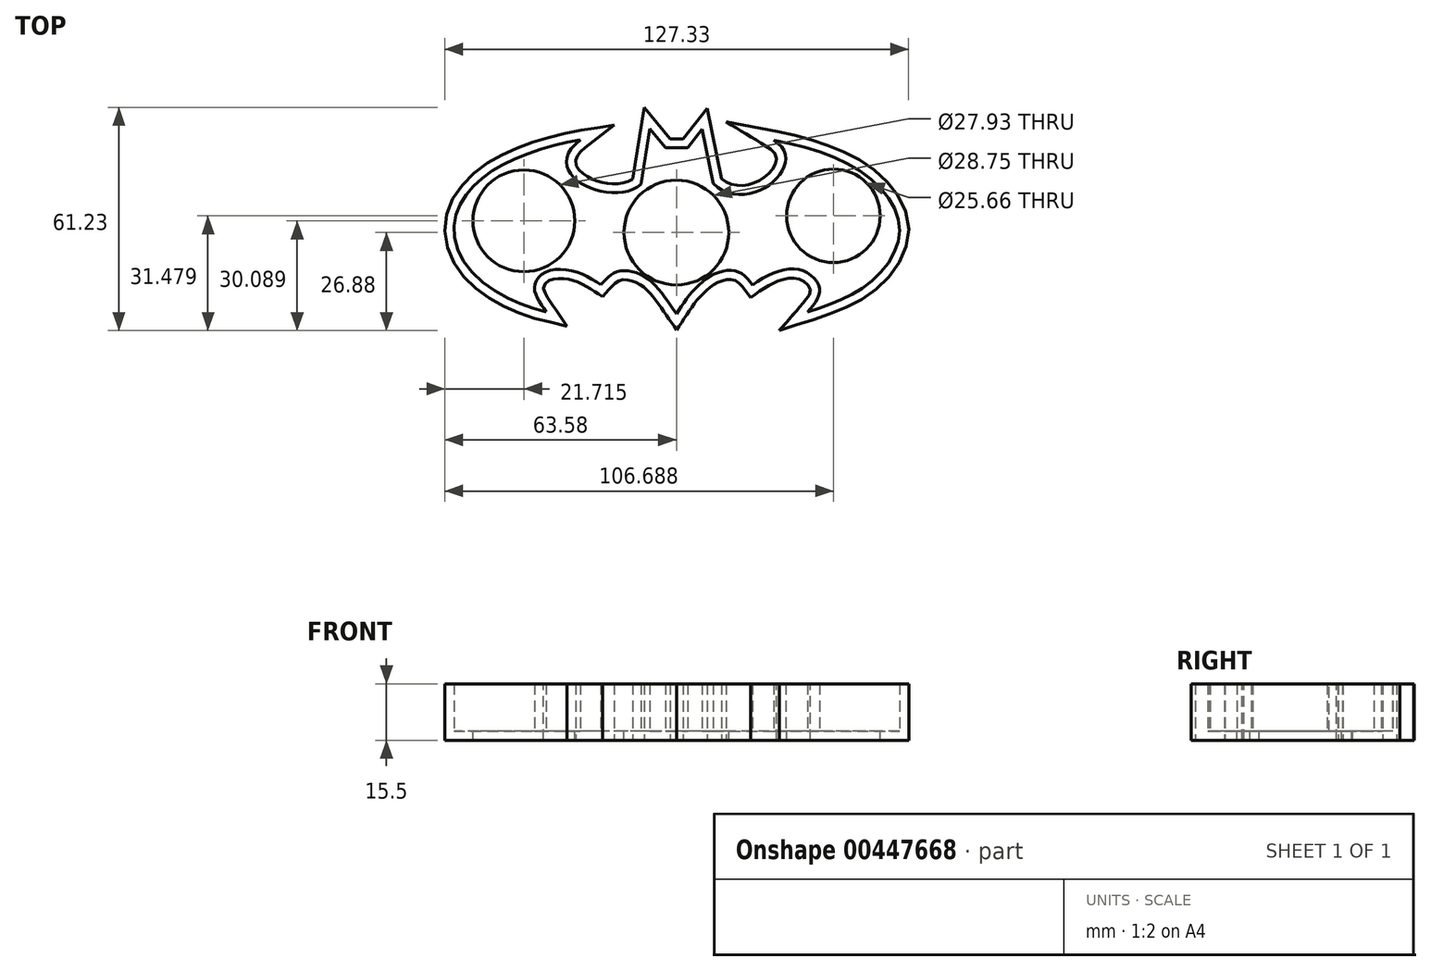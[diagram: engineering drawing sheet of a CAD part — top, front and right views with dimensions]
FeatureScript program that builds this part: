
annotation { "Feature Type Name" : "Feature", "Feature Type Description" : "" }
export const myFeature = defineFeature(function(context is Context, id is Id, definition is map)
    precondition{}
    {
        {
            var Q0;
            Q0=qCreatedBy(makeId("Top.planeOp"),FACE);
            var sketch = newSketch(context, id + "F0", { "sketchPlane" : qUnion([Q0])});
            skLineSegment(sketch, "E0", {"start": v(-2.96, 13.62) * mm, "end": v(3.07, 13.62) * mm});
            skLineSegment(sketch, "E1", {"start": v(7.09, 18.7) * mm, "end": v(3.07, 13.62) * mm});
            skLineSegment(sketch, "E2", {"start": v(-7.25, 18.84) * mm, "end": v(-2.96, 13.62) * mm});
            skLineSegment(sketch, "E3", {"start": v(7.09, 18.7) * mm, "end": v(10.04, 3.84) * mm});
            skLineSegment(sketch, "E4", {"start": v(-7.25, 18.84) * mm, "end": v(-9.66, 3.7) * mm});
            skFitSpline(sketch, "E5", {"points": [v(-9.66, 3.7) * mm, v(-26.35, 15.88) * mm], "startDerivative": vector(-23.41, -20.9) * mm, "endDerivative": vector(37.32, 29.12) * mm});
            skFitSpline(sketch, "E6", {"points": [v(10.04, 3.84) * mm, v(26.7, 15.74) * mm], "startDerivative": vector(29.47, -28.28) * mm, "endDerivative": vector(-31.58, 19.28) * mm});
            skFitSpline(sketch, "E7", {"points": [v(26.7, 15.74) * mm, v(53.14, 5.3) * mm, v(61.23, -9.78) * mm, v(52.21, -24.08) * mm, v(36.04, -31.36) * mm], "startDerivative": vector(99.78, -18.86) * mm, "endDerivative": vector(-72.14, -23.28) * mm});
            skFitSpline(sketch, "E8", {"points": [v(36.04, -31.36) * mm, v(39.31, -25.36) * mm, v(34.1, -19.88) * mm, v(20.9, -24) * mm], "startDerivative": vector(17.69, 20.3) * mm, "endDerivative": vector(-31.55, -22.7) * mm});
            skFitSpline(sketch, "E9", {"points": [v(20.9, -24) * mm, v(16.93, -20.4) * mm, v(10.84, -20.83) * mm, v(4.44, -25.76) * mm, v(0, -31.92) * mm], "startDerivative": vector(-15.97, 20.45) * mm, "endDerivative": vector(-15.43, -23.5) * mm});
            skFitSpline(sketch, "E10", {"points": [v(0, -31.92) * mm, v(-7.8, -22.35) * mm, v(-15.99, -20.26) * mm, v(-20.71, -23.94) * mm], "startDerivative": vector(-18.57, 26.13) * mm, "endDerivative": vector(-14.9, -16.95) * mm});
            skFitSpline(sketch, "E11", {"points": [v(-20.71, -23.94) * mm, v(-28.16, -20.2) * mm, v(-35.94, -20.5) * mm, v(-38.9, -23.94) * mm, v(-38.27, -27.34) * mm, v(-35.78, -31.38) * mm], "startDerivative": vector(-28.94, 18.52) * mm, "endDerivative": vector(15.1, -22.1) * mm});
            skFitSpline(sketch, "E12", {"points": [v(-35.78, -31.38) * mm, v(-46.5, -27.5) * mm, v(-56.92, -19.57) * mm, v(-60.97, -10.4) * mm, v(-59.88, -2.93) * mm, v(-55.21, 3.6) * mm, v(-47.9, 8.88) * mm, v(-37.18, 13.23) * mm, v(-26.35, 15.88) * mm], "startDerivative": vector(-82.47, 19.77) * mm, "endDerivative": vector(84, 13.74) * mm});
            skSolve(sketch);
        }
        {
            var Q0;
            Q0=makeQuery(id+"F0.imprint","IMPRINT",FACE,{"disambiguationData":[TD([[makeQuery(id+"F0.imprint","IMPRINT",EDGE,{"derivedFrom":sQuery(id+"F0.wireOp",EDGE,"E0")}),-1.0]])]});
            extrude(context, id + "F1", {"entities" : qUnion([Q0]), "depth" : 13 * mm});
        }
        {
            var Q0;
            Q0=makeQuery(id+"F1.opExtrude","CAP_FACE",FACE,{"disambiguationData":[OSD([sQuery(id+"F0.wireOp",EDGE,"E0"),sQuery(id+"F0.wireOp",EDGE,"E1"),sQuery(id+"F0.wireOp",EDGE,"E2"),sQuery(id+"F0.wireOp",EDGE,"E3"),sQuery(id+"F0.wireOp",EDGE,"E4"),sQuery(id+"F0.wireOp",EDGE,"E5"),sQuery(id+"F0.wireOp",EDGE,"E6"),sQuery(id+"F0.wireOp",EDGE,"E7"),sQuery(id+"F0.wireOp",EDGE,"E8"),sQuery(id+"F0.wireOp",EDGE,"E9"),sQuery(id+"F0.wireOp",EDGE,"E10"),sQuery(id+"F0.wireOp",EDGE,"E11"),sQuery(id+"F0.wireOp",EDGE,"E12")])],"isStart":false});
            shell(context, id + "F2", {"entities" : qUnion([Q0]), "thickness" : 2.5 * mm, "oppositeDirection" : true});
        }
        {
            var Q0;
            Q0=qCreatedBy(makeId("Top.planeOp"),FACE);
            var sketch = newSketch(context, id + "F3", { "sketchPlane" : qUnion([Q0])});
            skCircle(sketch, "E13", {"center": v(43.1, -5.02) * mm, "radius": 12.83 * mm});
            skCircle(sketch, "E14", {"center": v(0, -9.62) * mm, "radius": 14.38 * mm});
            skCircle(sketch, "E15", {"center": v(-41.87, -6.41) * mm, "radius": 13.96 * mm});
            skSolve(sketch);
        }
        {
            var Q0;
            Q0 = qSketchRegion(id + "F3", true);
            extrude(context, id + "F4", {"entities" : qUnion([Q0]), "operationType" : NewBodyOperationType.REMOVE, "oppositeDirection" : true, "depth" : 25 * mm});
        }
    });
